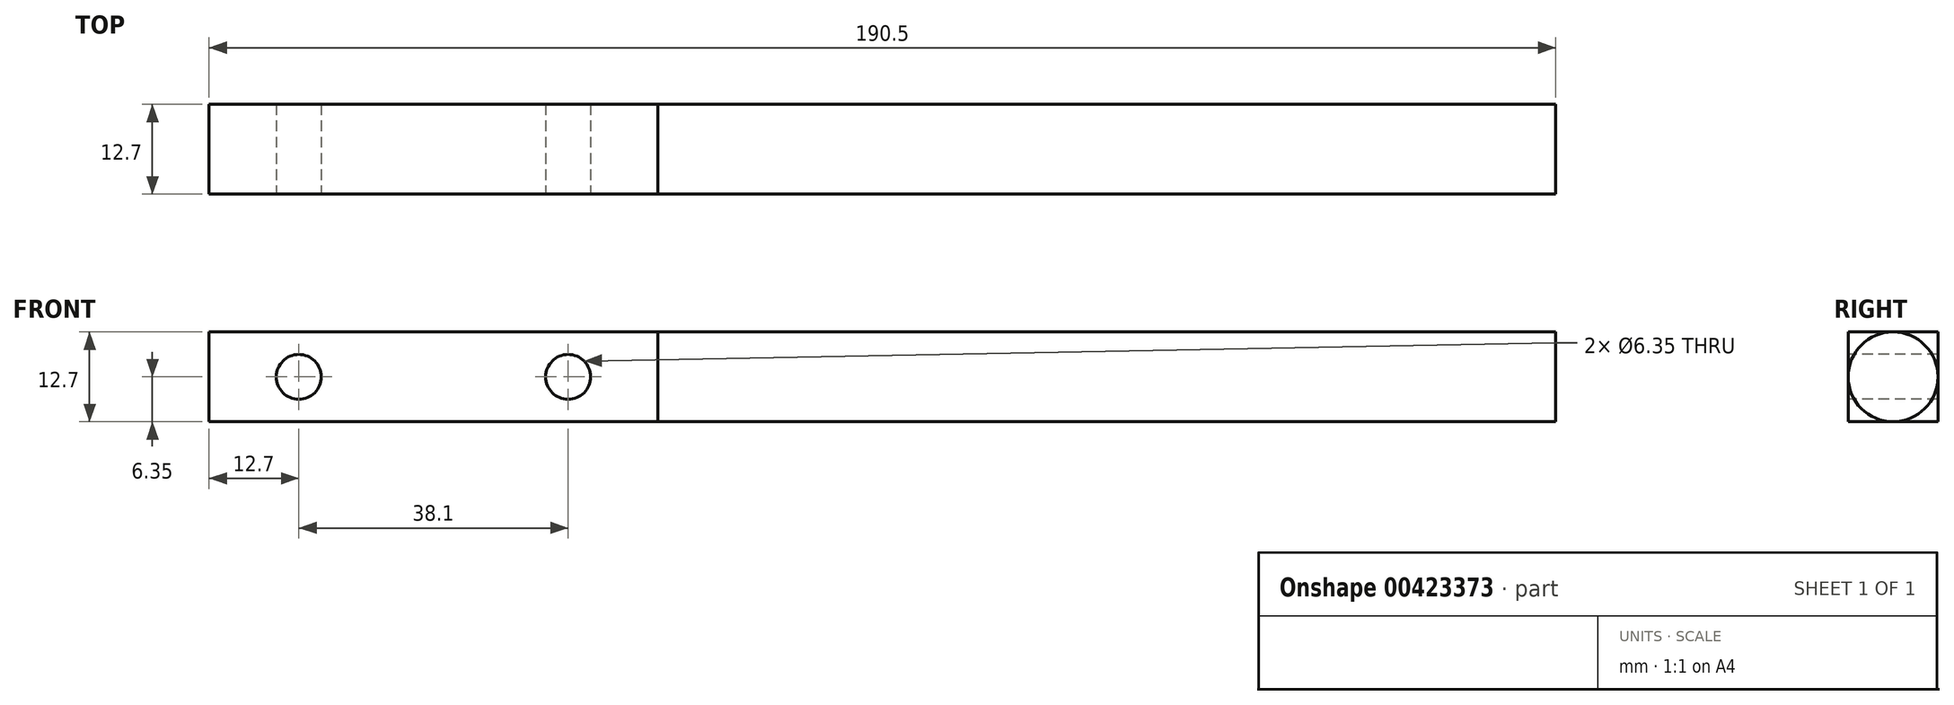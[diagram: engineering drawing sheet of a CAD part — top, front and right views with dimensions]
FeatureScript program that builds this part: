
annotation { "Feature Type Name" : "Feature", "Feature Type Description" : "" }
export const myFeature = defineFeature(function(context is Context, id is Id, definition is map)
    precondition{}
    {
        {
            var Q0;
            Q0=qCreatedBy(makeId("Front.planeOp"),FACE);
            var sketch = newSketch(context, id + "F0", { "sketchPlane" : qUnion([Q0])});
            skLineSegment(sketch, "E0.bottom", {"start": v(-63.5, 6.35) * mm, "end": v(0, 6.35) * mm});
            skLineSegment(sketch, "E0.top", {"start": v(-63.5, -6.35) * mm, "end": v(0, -6.35) * mm});
            skLineSegment(sketch, "E0.left", {"start": v(-63.5, 6.35) * mm, "end": v(-63.5, -6.35) * mm});
            skLineSegment(sketch, "E0.right", {"start": v(0, 6.35) * mm, "end": v(0, -6.35) * mm});
            skSolve(sketch);
        }
        {
            var Q0;
            Q0 = qSketchRegion(id + "F0", true);
            extrude(context, id + "F1", {"entities" : qUnion([Q0]), "endBound" : BoundingType.SYMMETRIC, "depth" : 12.7 * mm});
        }
        {
            var Q0;
            Q0=makeQuery(id+"F1.opExtrude","SWEPT_FACE",FACE,{"disambiguationData":[OSD([sQuery(id+"F0.wireOp",EDGE,"E0.right")])]});
            var sketch = newSketch(context, id + "F2", { "sketchPlane" : qUnion([Q0])});
            skCircle(sketch, "E1", {"center": v(0, 0) * mm, "radius": 6.35 * mm});
            skSolve(sketch);
        }
        {
            var Q0;
            Q0 = qSketchRegion(id + "F2", true);
            extrude(context, id + "F3", {"entities" : qUnion([Q0]), "operationType" : NewBodyOperationType.ADD, "depth" : 127 * mm});
        }
        {
            var Q0;
            Q0=makeQuery(id+"F1.opExtrude","CAP_FACE",FACE,{"disambiguationData":[OSD([sQuery(id+"F0.wireOp",EDGE,"E0.bottom"),sQuery(id+"F0.wireOp",EDGE,"E0.top"),sQuery(id+"F0.wireOp",EDGE,"E0.left"),sQuery(id+"F0.wireOp",EDGE,"E0.right")])],"isStart":false});
            var sketch = newSketch(context, id + "F4", { "sketchPlane" : qUnion([Q0])});
            skCircle(sketch, "E2", {"center": v(-50.8, 0) * mm, "radius": 3.18 * mm});
            skCircle(sketch, "E3", {"center": v(-12.7, 0) * mm, "radius": 3.18 * mm});
            skSolve(sketch);
        }
        {
            var Q0;
            Q0 = qSketchRegion(id + "F4", true);
            extrude(context, id + "F5", {"entities" : qUnion([Q0]), "operationType" : NewBodyOperationType.REMOVE, "endBound" : BoundingType.THROUGH_ALL, "oppositeDirection" : true, "depth" : 25.4 * mm});
        }
    });
